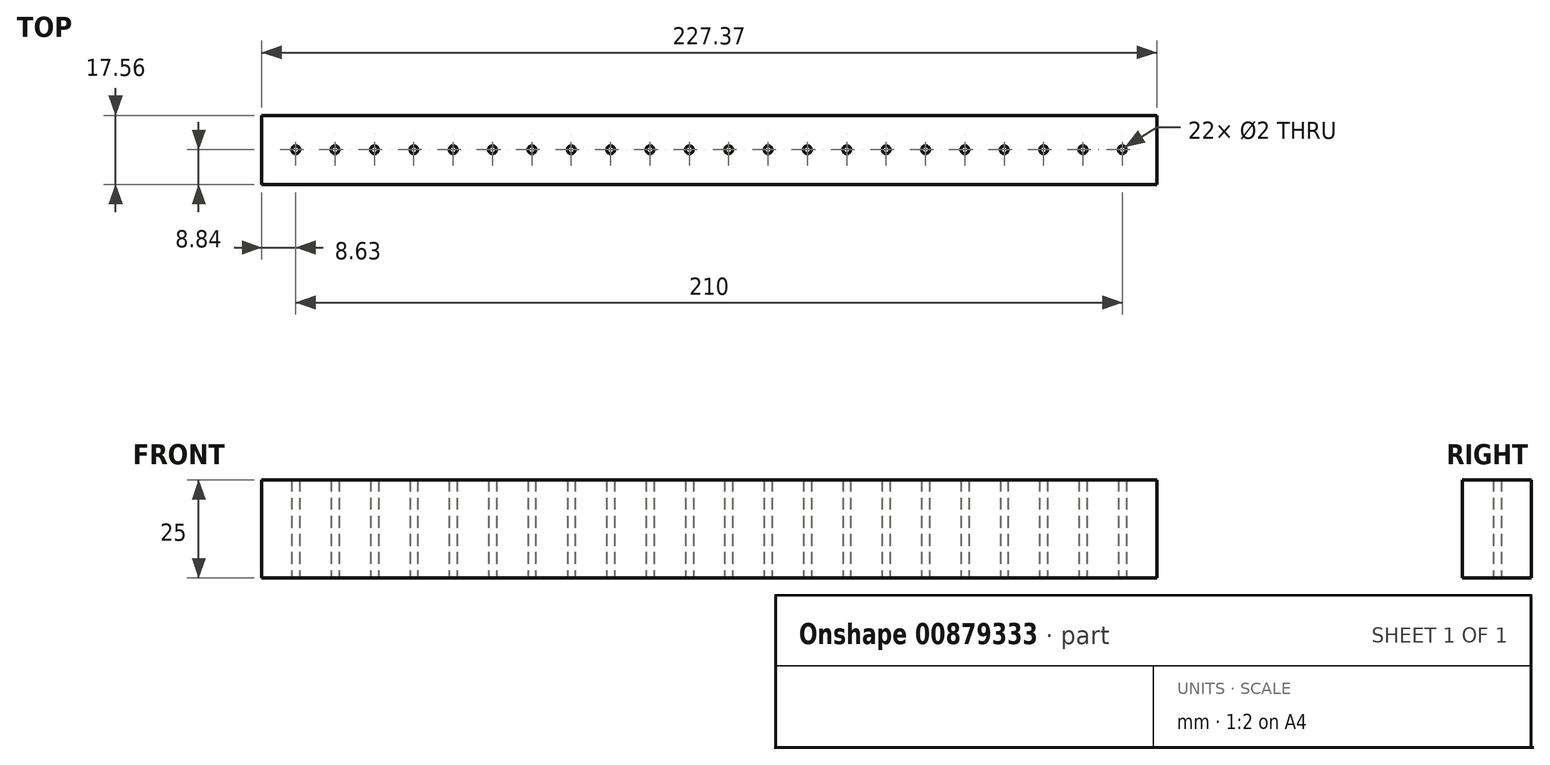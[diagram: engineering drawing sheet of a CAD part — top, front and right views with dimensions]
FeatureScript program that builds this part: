
annotation { "Feature Type Name" : "Feature", "Feature Type Description" : "" }
export const myFeature = defineFeature(function(context is Context, id is Id, definition is map)
    precondition{}
    {
        {
            var Q0;
            Q0=qCreatedBy(makeId("Top.planeOp"),FACE);
            var sketch = newSketch(context, id + "F0", { "sketchPlane" : qUnion([Q0])});
            skCircle(sketch, "E0", {"center": v(0, 0) * mm, "radius": 1 * mm});
            skCircle(sketch, "E1.1.0.0", {"center": v(10, 0) * mm, "radius": 1 * mm});
            skCircle(sketch, "E1.2.0.0", {"center": v(20, 0) * mm, "radius": 1 * mm});
            skCircle(sketch, "E1.3.0.0", {"center": v(30, 0) * mm, "radius": 1 * mm});
            skCircle(sketch, "E1.4.0.0", {"center": v(40, 0) * mm, "radius": 1 * mm});
            skCircle(sketch, "E1.5.0.0", {"center": v(50, 0) * mm, "radius": 1 * mm});
            skCircle(sketch, "E1.6.0.0", {"center": v(60, 0) * mm, "radius": 1 * mm});
            skCircle(sketch, "E1.7.0.0", {"center": v(70, 0) * mm, "radius": 1 * mm});
            skCircle(sketch, "E1.8.0.0", {"center": v(80, 0) * mm, "radius": 1 * mm});
            skCircle(sketch, "E1.9.0.0", {"center": v(90, 0) * mm, "radius": 1 * mm});
            skCircle(sketch, "E1.10.0.0", {"center": v(100, 0) * mm, "radius": 1 * mm});
            skCircle(sketch, "E1.11.0.0", {"center": v(110, 0) * mm, "radius": 1 * mm});
            skCircle(sketch, "E1.12.0.0", {"center": v(120, 0) * mm, "radius": 1 * mm});
            skCircle(sketch, "E1.13.0.0", {"center": v(130, 0) * mm, "radius": 1 * mm});
            skCircle(sketch, "E1.14.0.0", {"center": v(140, 0) * mm, "radius": 1 * mm});
            skCircle(sketch, "E1.15.0.0", {"center": v(150, 0) * mm, "radius": 1 * mm});
            skCircle(sketch, "E1.16.0.0", {"center": v(160, 0) * mm, "radius": 1 * mm});
            skCircle(sketch, "E1.17.0.0", {"center": v(170, 0) * mm, "radius": 1 * mm});
            skCircle(sketch, "E1.18.0.0", {"center": v(180, 0) * mm, "radius": 1 * mm});
            skCircle(sketch, "E1.19.0.0", {"center": v(190, 0) * mm, "radius": 1 * mm});
            skCircle(sketch, "E1.20.0.0", {"center": v(200, 0) * mm, "radius": 1 * mm});
            skCircle(sketch, "E1.21.0.0", {"center": v(210, 0) * mm, "radius": 1 * mm});
            skLineSegment(sketch, "E1.direction1", {"start": v(0, 0) * mm, "end": v(10, 0) * mm, "construction": true});
            skLineSegment(sketch, "E2.bottom", {"start": v(-8.63, 8.72) * mm, "end": v(218.74, 8.72) * mm});
            skLineSegment(sketch, "E2.top", {"start": v(-8.63, -8.84) * mm, "end": v(218.74, -8.84) * mm});
            skLineSegment(sketch, "E2.left", {"start": v(-8.63, 8.72) * mm, "end": v(-8.63, -8.84) * mm});
            skLineSegment(sketch, "E2.right", {"start": v(218.74, 8.72) * mm, "end": v(218.74, -8.84) * mm});
            skSolve(sketch);
        }
        {
            var Q0;
            Q0=makeQuery(id+"F0.imprint","IMPRINT",FACE,{"disambiguationData":[TD([[makeQuery(id+"F0.imprint","IMPRINT",EDGE,{"derivedFrom":sQuery(id+"F0.wireOp",EDGE,"E0")}),-1.0]])]});
            extrude(context, id + "F1", {"entities" : qUnion([Q0]), "depth" : 25 * mm, "offsetDistance" : 25 * mm});
        }
    });
